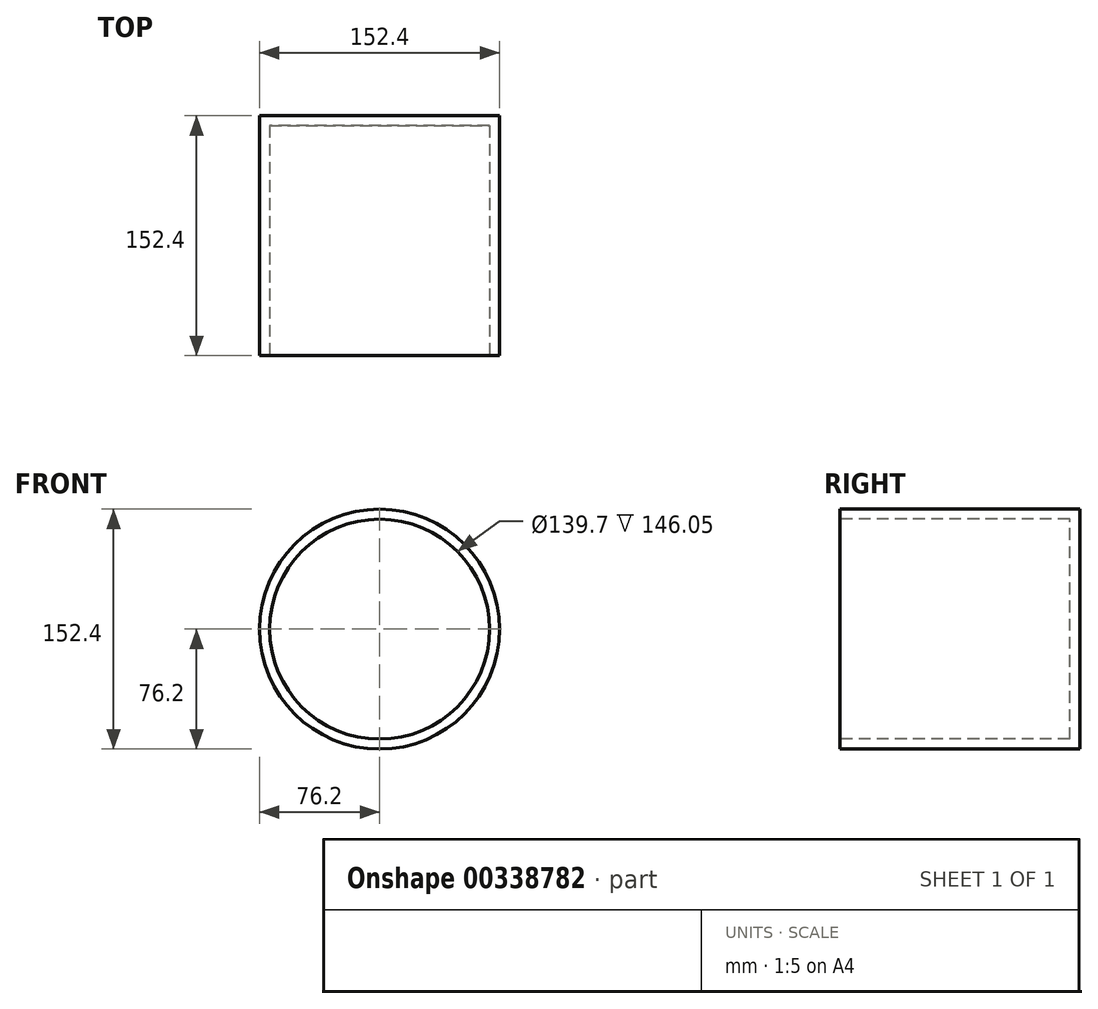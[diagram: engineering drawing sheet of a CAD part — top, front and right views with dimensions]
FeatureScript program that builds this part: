
annotation { "Feature Type Name" : "Feature", "Feature Type Description" : "" }
export const myFeature = defineFeature(function(context is Context, id is Id, definition is map)
    precondition{}
    {
        {
            var Q0;
            Q0=qCreatedBy(makeId("Front.planeOp"),FACE);
            var sketch = newSketch(context, id + "F0", { "sketchPlane" : qUnion([Q0])});
            skCircle(sketch, "E0", {"center": v(0, 0) * mm, "radius": 76.2 * mm});
            skSolve(sketch);
        }
        {
            var Q0;
            Q0=makeQuery(id+"F0.imprint","IMPRINT",FACE,{"disambiguationData":[TD([[makeQuery(id+"F0.imprint","IMPRINT",EDGE,{"derivedFrom":sQuery(id+"F0.wireOp",EDGE,"E0")}),1.0]])]});
            extrude(context, id + "F1", {"entities" : qUnion([Q0]), "oppositeDirection" : true, "depth" : 152.4 * mm});
        }
        {
            var Q0;
            Q0=makeQuery(id+"F1.opExtrude","CAP_FACE",FACE,{"disambiguationData":[OSD([sQuery(id+"F0.wireOp",EDGE,"E0")])],"isStart":true});
            shell(context, id + "F2", {"entities" : qUnion([Q0]), "thickness" : 6.35 * mm});
        }
    });
